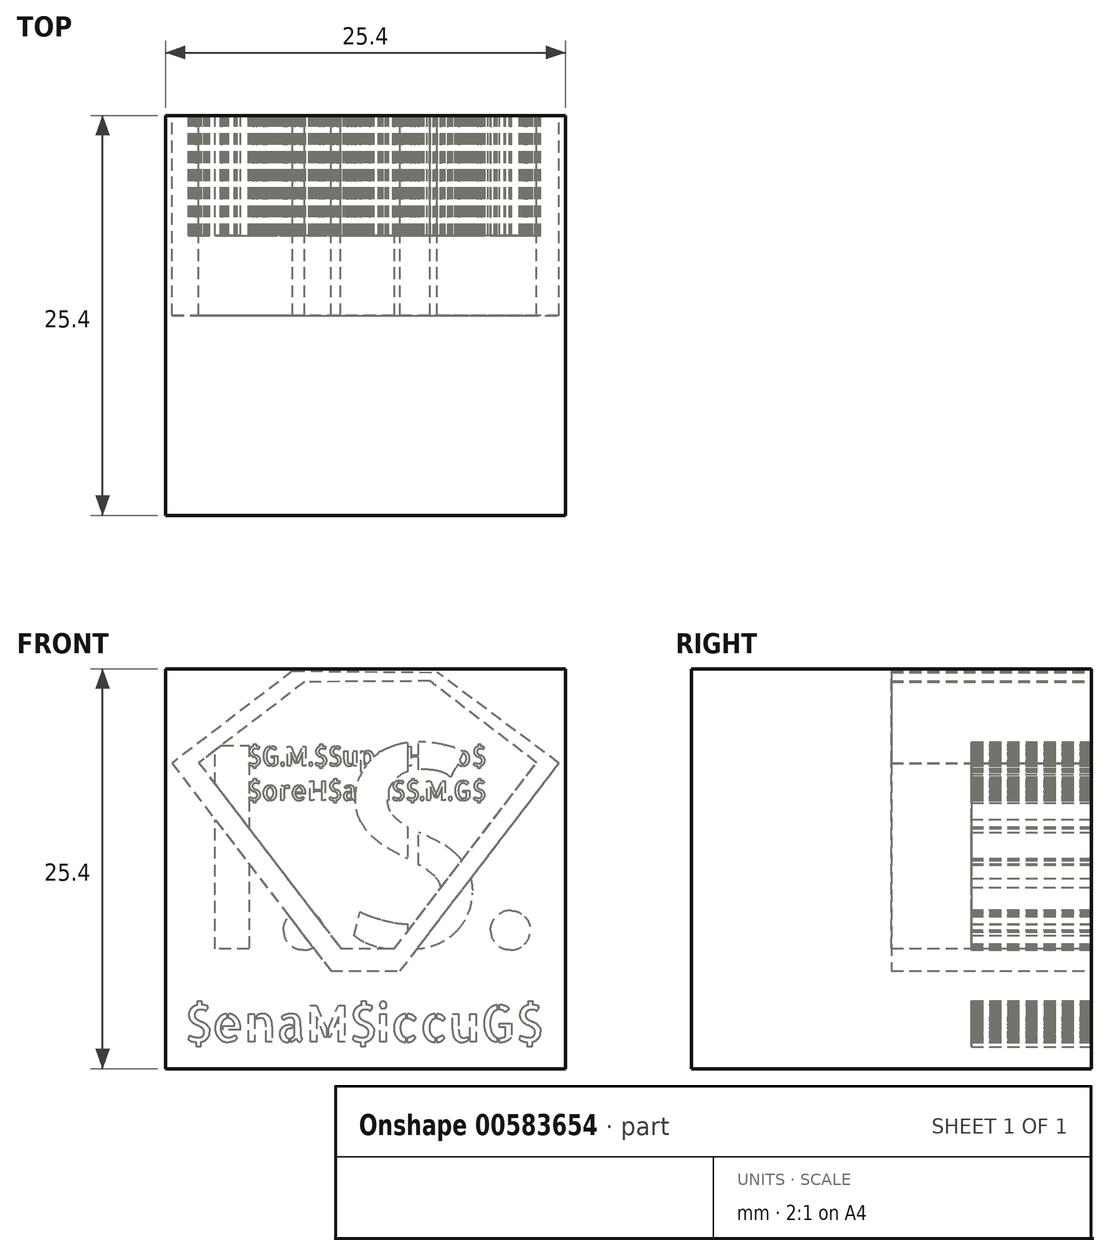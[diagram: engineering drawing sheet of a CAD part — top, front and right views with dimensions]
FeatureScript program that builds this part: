
annotation { "Feature Type Name" : "Feature", "Feature Type Description" : "" }
export const myFeature = defineFeature(function(context is Context, id is Id, definition is map)
    precondition{}
    {
        {
            var Q0;
            Q0=qCreatedBy(makeId("Front.planeOp"),FACE);
            var sketch = newSketch(context, id + "F0", { "sketchPlane" : qUnion([Q0])});
            skLineSegment(sketch, "E0.bottom", {"start": v(12.7, 12.7) * mm, "end": v(-12.7, 12.7) * mm});
            skLineSegment(sketch, "E0.top", {"start": v(12.7, -12.7) * mm, "end": v(-12.7, -12.7) * mm});
            skLineSegment(sketch, "E0.left", {"start": v(12.7, 12.7) * mm, "end": v(12.7, -12.7) * mm});
            skLineSegment(sketch, "E0.right", {"start": v(-12.7, 12.7) * mm, "end": v(-12.7, -12.7) * mm});
            skPoint(sketch, "E0.middle", {"position": v(0, 0) * mm});
            skSolve(sketch);
        }
        {
            var Q0;
            Q0 = qSketchRegion(id + "F0", true);
            extrude(context, id + "F1", {"entities" : qUnion([Q0]), "depth" : 25.4 * mm, "offsetDistance" : 25.4 * mm});
        }
        {
            var Q0;
            Q0=qCreatedBy(makeId("Front.planeOp"),FACE);
            var sketch = newSketch(context, id + "F2", { "sketchPlane" : qUnion([Q0])});
            skLineSegment(sketch, "E1", {"start": v(-4.62, 12.56) * mm, "end": v(-12.3, 6.7) * mm});
            skLineSegment(sketch, "E2", {"start": v(-12.3, 6.7) * mm, "end": v(-2.2, -6.5) * mm});
            skLineSegment(sketch, "E3", {"start": v(-2.2, -6.5) * mm, "end": v(0, -6.5) * mm});
            skLineSegment(sketch, "E4", {"start": v(0, -6.5) * mm, "end": v(2.2, -6.5) * mm});
            skLineSegment(sketch, "E5", {"start": v(2.2, -6.5) * mm, "end": v(12.3, 6.7) * mm});
            skLineSegment(sketch, "E6", {"start": v(12.3, 6.7) * mm, "end": v(4.55, 12.47) * mm});
            skLineSegment(sketch, "E7", {"start": v(-4.62, 12.56) * mm, "end": v(4.55, 12.47) * mm});
            skLineSegment(sketch, "E8", {"start": v(-3.87, 11.87) * mm, "end": v(-10.6, 6.73) * mm});
            skLineSegment(sketch, "E9", {"start": v(-10.6, 6.73) * mm, "end": v(-1.57, -5.07) * mm});
            skLineSegment(sketch, "E10", {"start": v(-1.57, -5.07) * mm, "end": v(1.84, -5.07) * mm});
            skLineSegment(sketch, "E11", {"start": v(1.84, -5.07) * mm, "end": v(10.87, 6.73) * mm});
            skLineSegment(sketch, "E12", {"start": v(10.87, 6.73) * mm, "end": v(4.08, 11.91) * mm});
            skLineSegment(sketch, "E13", {"start": v(4.08, 11.91) * mm, "end": v(-3.87, 11.87) * mm});
            skLineSegment(sketch, "E14", {"start": v(-10.6, 6.73) * mm, "end": v(-12.3, 6.7) * mm});
            skLineSegment(sketch, "E15", {"start": v(-3.87, 11.87) * mm, "end": v(-4.62, 12.56) * mm});
            skLineSegment(sketch, "E16", {"start": v(4.08, 11.91) * mm, "end": v(4.55, 12.47) * mm});
            skLineSegment(sketch, "E17", {"start": v(10.87, 6.73) * mm, "end": v(12.3, 6.7) * mm});
            skLineSegment(sketch, "E18", {"start": v(1.84, -5.07) * mm, "end": v(2.2, -6.5) * mm});
            skLineSegment(sketch, "E19", {"start": v(-1.57, -5.07) * mm, "end": v(-2.2, -6.5) * mm});
            skSolve(sketch);
        }
        {
            var Q0;
            Q0 = qSketchRegion(id + "F2", true);
            extrude(context, id + "F3", {"entities" : qUnion([Q0]), "operationType" : NewBodyOperationType.REMOVE, "depth" : 12.7 * mm, "offsetDistance" : 25.4 * mm});
        }
        {
            var Q0;
            Q0=qCreatedBy(makeId("Front.planeOp"),FACE);
            var sketch = newSketch(context, id + "F4", { "sketchPlane" : qUnion([Q0])});
            skText(sketch, "E20", { "text": "$enaM$iccuG$", "fontName": "AllertaStencil-Regular.ttf"});
            const initialGuessF4  = {"E20": [-0.0115, -0.01101, 1, 0, 0.00233]};
            skSetInitialGuess(sketch, initialGuessF4);
            skSolve(sketch);
        }
        {
            var Q0;
            Q0=qCreatedBy(makeId("Front.planeOp"),FACE);
            var sketch = newSketch(context, id + "F5", { "sketchPlane" : qUnion([Q0])});
            skText(sketch, "E21", { "text": "I.S.", "fontName": "AllertaStencil-Regular.ttf"});
            const initialGuessF5  = {"E21": [-0.0112, -0.0051, 1, 0, 0.01295]};
            skSetInitialGuess(sketch, initialGuessF5);
            skSolve(sketch);
        }
        {
            var Q0;
            Q0=qCreatedBy(makeId("Front.planeOp"),FACE);
            var sketch = newSketch(context, id + "F6", { "sketchPlane" : qUnion([Q0])});
            skText(sketch, "E22", { "text": "$G.M.$Supa$Hero$\n$oreH$apuS$.M.G$", "fontName": "AllertaStencil-Regular.ttf"});
            const initialGuessF6  = {"E22": [-0.00753, 0.00653, 1, 0, 0.00123]};
            skSetInitialGuess(sketch, initialGuessF6);
            skSolve(sketch);
        }
        {
            var Q0;
            Q0 = qSketchRegion(id + "F4", true);
            extrude(context, id + "F7", {"entities" : qUnion([Q0]), "operationType" : NewBodyOperationType.REMOVE, "depth" : 7.62 * mm, "offsetDistance" : 25.4 * mm});
        }
        {
            var Q0;
            Q0 = qSketchRegion(id + "F6", true);
            extrude(context, id + "F8", {"entities" : qUnion([Q0]), "operationType" : NewBodyOperationType.REMOVE, "depth" : 7.62 * mm, "offsetDistance" : 25.4 * mm});
        }
        {
            var Q0;
            Q0 = qSketchRegion(id + "F5", true);
            extrude(context, id + "F9", {"entities" : qUnion([Q0]), "operationType" : NewBodyOperationType.REMOVE, "depth" : 7.62 * mm, "offsetDistance" : 25.4 * mm});
        }
    });
